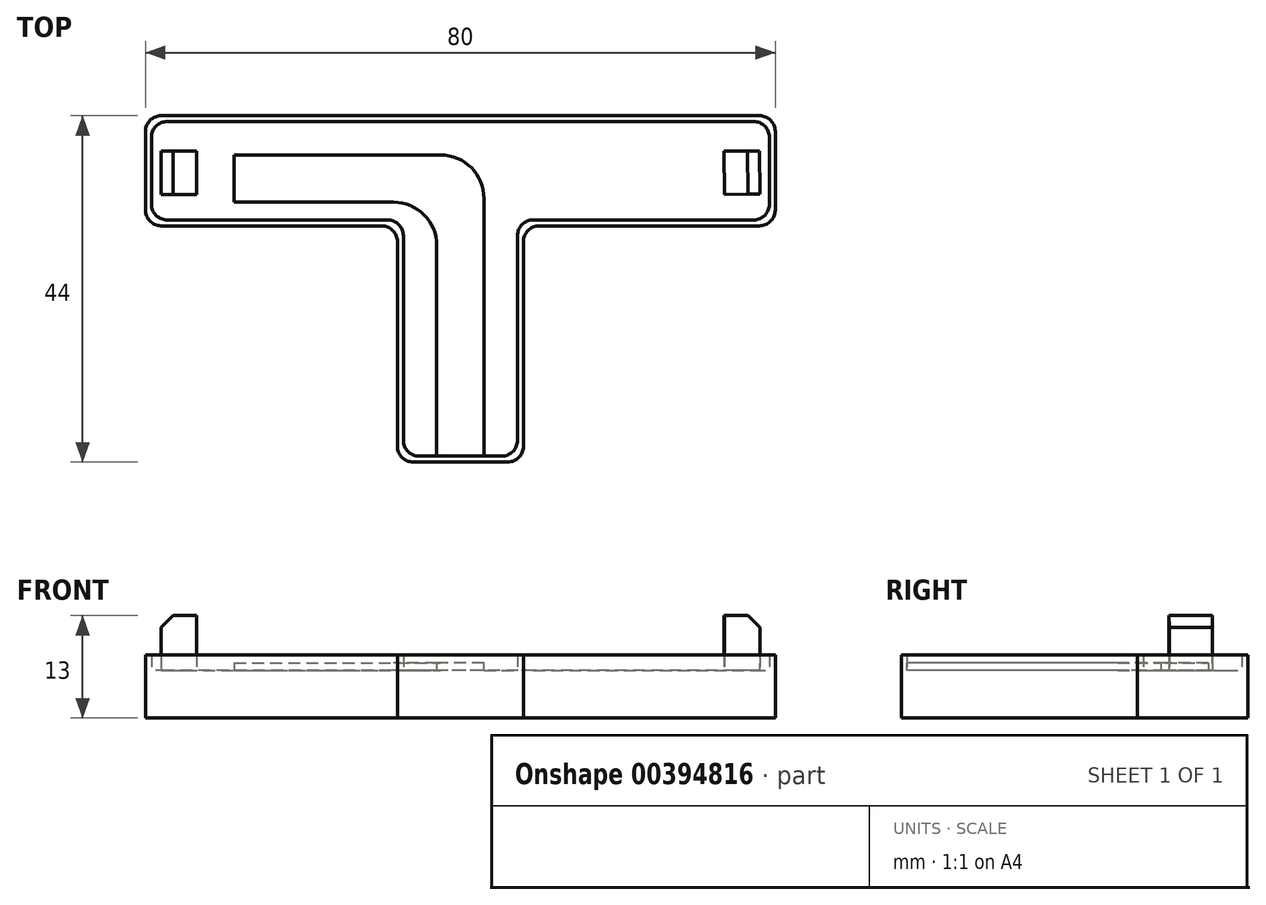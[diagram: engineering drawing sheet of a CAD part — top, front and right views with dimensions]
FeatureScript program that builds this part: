
annotation { "Feature Type Name" : "Feature", "Feature Type Description" : "" }
export const myFeature = defineFeature(function(context is Context, id is Id, definition is map)
    precondition{}
    {
        {
            var Q0;
            Q0=qCreatedBy(makeId("Top.planeOp"),FACE);
            var sketch = newSketch(context, id + "F0", { "sketchPlane" : qUnion([Q0])});
            skLineSegment(sketch, "E0", {"start": v(-12, 0) * mm, "end": v(-35, 0) * mm});
            skLineSegment(sketch, "E1", {"start": v(-37, 2) * mm, "end": v(-37, 12) * mm});
            skLineSegment(sketch, "E2", {"start": v(-35, 14) * mm, "end": v(35, 14) * mm});
            skLineSegment(sketch, "E3", {"start": v(37, 12) * mm, "end": v(37, 2) * mm});
            skLineSegment(sketch, "E4", {"start": v(6, -30) * mm, "end": v(-6, -30) * mm});
            skPoint(sketch, "E5.visualSharp", {"position": v(-37, 0) * mm});
            skArc(sketch, "E5.filletArc", {"start": v(-37, 2) * mm, "mid": v(-36.41, 0.59) * mm, "end": v(-35, 0) * mm});
            skPoint(sketch, "E6.visualSharp", {"position": v(-37, 14) * mm});
            skArc(sketch, "E6.filletArc", {"start": v(-35, 14) * mm, "mid": v(-36.41, 13.41) * mm, "end": v(-37, 12) * mm});
            skPoint(sketch, "E7.visualSharp", {"position": v(37, 14) * mm});
            skArc(sketch, "E7.filletArc", {"start": v(37, 12) * mm, "mid": v(36.41, 13.41) * mm, "end": v(35, 14) * mm});
            skPoint(sketch, "E8.visualSharp", {"position": v(37, 0) * mm});
            skArc(sketch, "E8.filletArc", {"start": v(35, 0) * mm, "mid": v(36.41, 0.59) * mm, "end": v(37, 2) * mm});
            skPoint(sketch, "E9.newPointA", {"position": v(0, 0) * mm});
            skPoint(sketch, "E10.newPointB", {"position": v(-10, 0) * mm});
            skLineSegment(sketch, "E11", {"start": v(-10, 0) * mm, "end": v(-38, 0) * mm});
            skLineSegment(sketch, "E12", {"start": v(-40, 2) * mm, "end": v(-40, 12) * mm});
            skLineSegment(sketch, "E13", {"start": v(-38, 14) * mm, "end": v(38, 14) * mm});
            skPoint(sketch, "E13.endSnap0", {"position": v(0, 14) * mm});
            skLineSegment(sketch, "E14", {"start": v(40, 12) * mm, "end": v(40, 2) * mm});
            skPoint(sketch, "E15.visualSharp", {"position": v(40, 14) * mm});
            skArc(sketch, "E15.filletArc", {"start": v(40, 12) * mm, "mid": v(39.41, 13.41) * mm, "end": v(38, 14) * mm});
            skPoint(sketch, "E16.visualSharp", {"position": v(40, 0) * mm});
            skArc(sketch, "E16.filletArc", {"start": v(38, 0) * mm, "mid": v(39.41, 0.59) * mm, "end": v(40, 2) * mm});
            skPoint(sketch, "E17.visualSharp", {"position": v(-40, 0) * mm});
            skArc(sketch, "E17.filletArc", {"start": v(-40, 2) * mm, "mid": v(-39.41, 0.59) * mm, "end": v(-38, 0) * mm});
            skPoint(sketch, "E18.visualSharp", {"position": v(-40, 14) * mm});
            skArc(sketch, "E18.filletArc", {"start": v(-38, 14) * mm, "mid": v(-39.41, 13.41) * mm, "end": v(-40, 12) * mm});
            skLineSegment(sketch, "E19", {"start": v(-10, 0) * mm, "end": v(-10, 0) * mm});
            skLineSegment(sketch, "E20", {"start": v(40, 0) * mm, "end": v(37, 0) * mm});
            skLineSegment(sketch, "E21", {"start": v(0, -30) * mm, "end": v(8, -30) * mm});
            skLineSegment(sketch, "E22", {"start": v(8, -28) * mm, "end": v(8, -2) * mm});
            skLineSegment(sketch, "E23.trimOffspring", {"start": v(35, 0) * mm, "end": v(38, 0) * mm});
            skLineSegment(sketch, "E24", {"start": v(10, 0) * mm, "end": v(38, 0) * mm});
            skArc(sketch, "E25.filletArc", {"start": v(10, 0) * mm, "mid": v(8.59, -0.59) * mm, "end": v(8, -2) * mm});
            skLineSegment(sketch, "E26", {"start": v(-8, -2) * mm, "end": v(-8, -28) * mm});
            skPoint(sketch, "E27.visualSharp", {"position": v(-8, -30) * mm});
            skArc(sketch, "E27.filletArc", {"start": v(-8, -28) * mm, "mid": v(-7.41, -29.41) * mm, "end": v(-6, -30) * mm});
            skPoint(sketch, "E28.visualSharp", {"position": v(8, -30) * mm});
            skArc(sketch, "E28.filletArc", {"start": v(6, -30) * mm, "mid": v(7.41, -29.41) * mm, "end": v(8, -28) * mm});
            skPoint(sketch, "E29.visualSharp", {"position": v(-8, 0) * mm});
            skArc(sketch, "E29.filletArc", {"start": v(-8, -2) * mm, "mid": v(-8.59, -0.59) * mm, "end": v(-10, 0) * mm});
            skSolve(sketch);
        }
        {
            var Q0;
            Q0 = qSketchRegion(id + "F0", true);
            extrude(context, id + "F1", {"entities" : qUnion([Q0]), "depth" : 6 * mm});
        }
        {
            var Q0;
            Q0=makeQuery(id+"F1.opExtrude","CAP_FACE",FACE,{"disambiguationData":[OSD([sQuery(id+"F0.wireOp",EDGE,"KrgK9lRR-1sEZ-YcQp-O3oG-SHxgb29owZ0h"),sQuery(id+"F0.wireOp",EDGE,"E0"),sQuery(id+"F0.wireOp",EDGE,"E1"),sQuery(id+"F0.wireOp",EDGE,"E2"),sQuery(id+"F0.wireOp",EDGE,"E3"),sQuery(id+"F0.wireOp",EDGE,"eoUHOFyy-lQIt-8kjD-7oxf-nCLPdvyQU6Ic"),sQuery(id+"F0.wireOp",EDGE,"2H0jnYMO-rJTe-XpiU-m9ek-4oq2zpUAxpcV"),sQuery(id+"F0.wireOp",EDGE,"E4"),sQuery(id+"F0.wireOp",EDGE,"E5.filletArc"),sQuery(id+"F0.wireOp",EDGE,"E6.filletArc"),sQuery(id+"F0.wireOp",EDGE,"E7.filletArc"),sQuery(id+"F0.wireOp",EDGE,"E8.filletArc"),sQuery(id+"F0.wireOp",EDGE,"E9.filletArc"),sQuery(id+"F0.wireOp",EDGE,"E10.filletArc"),sQuery(id+"F0.wireOp",EDGE,"4ed553e5-42bd-4c59-8323-b41fe6fd0794.filletArc"),sQuery(id+"F0.wireOp",EDGE,"28c6359a-0f53-4484-972b-61d877849d50.filletArc")])],"isStart":false});
            var sketch = newSketch(context, id + "F2", { "sketchPlane" : qUnion([Q0])});
            skPoint(sketch, "E30.visualSharp", {"position": v(-3, 9) * mm});
            skLineSegment(sketch, "E31", {"start": v(-3, -30) * mm, "end": v(3, -30) * mm});
            skLineSegment(sketch, "E32", {"start": v(-28.75, 9) * mm, "end": v(-2.5, 9) * mm});
            skLineSegment(sketch, "E33", {"start": v(-28.75, 3) * mm, "end": v(-8.5, 3) * mm});
            skLineSegment(sketch, "E34", {"start": v(3, 3.5) * mm, "end": v(3, -30) * mm});
            skLineSegment(sketch, "E35", {"start": v(-3, -2.5) * mm, "end": v(-3, -30) * mm});
            skLineSegment(sketch, "E36", {"start": v(3, -30) * mm, "end": v(-3, -30) * mm});
            skPoint(sketch, "E37.visualSharp", {"position": v(3, 9) * mm});
            skPoint(sketch, "E38.visualSharp", {"position": v(-3, 3) * mm});
            skLineSegment(sketch, "E39", {"start": v(-28.75, 9) * mm, "end": v(-28.75, 3) * mm});
            skPoint(sketch, "E40.orphan", {"position": v(-33, 3) * mm});
            skPoint(sketch, "E41.end.orphan", {"position": v(-33, 9) * mm});
            skArc(sketch, "E42", {"start": v(-7.98, 3) * mm, "mid": v(-7.98, 2.99) * mm, "end": v(-7.97, 2.97) * mm});
            skArc(sketch, "E43.trimOffspring", {"start": v(3, 3.5) * mm, "mid": v(1.39, 7.39) * mm, "end": v(-2.5, 9) * mm});
            skArc(sketch, "E44", {"start": v(-3, -2.5) * mm, "mid": v(-4.61, 1.39) * mm, "end": v(-8.5, 3) * mm});
            skSolve(sketch);
        }
        {
            var Q0;
            Q0=makeQuery(id+"F2.imprint","IMPRINT",FACE,{"disambiguationData":[TD([[makeQuery(id+"F2.imprint","IMPRINT",EDGE,{"derivedFrom":sQuery(id+"F2.wireOp",EDGE,"E32")}),-1.0]])]});
            extrude(context, id + "F3", {"entities" : qUnion([Q0]), "operationType" : NewBodyOperationType.ADD, "depth" : 1 * mm});
        }
        {
            var Q0;
            Q0=makeQuery(id+"F1.opExtrude","CAP_FACE",FACE,{"disambiguationData":[OSD([sQuery(id+"F0.wireOp",EDGE,"eoUHOFyy-lQIt-8kjD-7oxf-nCLPdvyQU6Ic"),sQuery(id+"F0.wireOp",EDGE,"2H0jnYMO-rJTe-XpiU-m9ek-4oq2zpUAxpcV"),sQuery(id+"F0.wireOp",EDGE,"E4"),sQuery(id+"F0.wireOp",EDGE,"E9.filletArc"),sQuery(id+"F0.wireOp",EDGE,"E10.filletArc"),sQuery(id+"F0.wireOp",EDGE,"4ed553e5-42bd-4c59-8323-b41fe6fd0794.filletArc"),sQuery(id+"F0.wireOp",EDGE,"28c6359a-0f53-4484-972b-61d877849d50.filletArc"),sQuery(id+"F0.wireOp",EDGE,"ouvHfpLu-oJne-QARU-IrEs-jNbR7pRuR2ui"),sQuery(id+"F0.wireOp",EDGE,"E11"),sQuery(id+"F0.wireOp",EDGE,"E12"),sQuery(id+"F0.wireOp",EDGE,"E13"),sQuery(id+"F0.wireOp",EDGE,"E14"),sQuery(id+"F0.wireOp",EDGE,"E15.filletArc"),sQuery(id+"F0.wireOp",EDGE,"E16.filletArc"),sQuery(id+"F0.wireOp",EDGE,"E17.filletArc"),sQuery(id+"F0.wireOp",EDGE,"E18.filletArc")])],"isStart":false});
            var sketch = newSketch(context, id + "F4", { "sketchPlane" : qUnion([Q0])});
            skLineSegment(sketch, "E45", {"start": v(0, 0) * mm, "end": v(35, 0) * mm});
            skLineSegment(sketch, "E46", {"start": v(35, 0) * mm, "end": v(40, 0) * mm});
            skLineSegment(sketch, "E47", {"start": v(40, 0) * mm, "end": v(38, 0) * mm});
            skPoint(sketch, "E48.endSnap0", {"position": v(38.04, 5.65) * mm});
            skLineSegment(sketch, "E49", {"start": v(38.04, 4.03) * mm, "end": v(35.24, 4) * mm});
            skPoint(sketch, "E50.orphan", {"position": v(37.9, 11.5) * mm});
            skLineSegment(sketch, "E51", {"start": v(38.04, 4.03) * mm, "end": v(37.97, 9.53) * mm});
            skLineSegment(sketch, "E52", {"start": v(37.97, 9.53) * mm, "end": v(35.17, 9.5) * mm});
            skLineSegment(sketch, "E53", {"start": v(0, 0) * mm, "end": v(-35, 0) * mm});
            skLineSegment(sketch, "E54", {"start": v(-35, 0) * mm, "end": v(-40.02, 0) * mm});
            skLineSegment(sketch, "E55", {"start": v(-40.02, 0) * mm, "end": v(-38.02, 0) * mm});
            skLineSegment(sketch, "E56", {"start": v(-38, 4) * mm, "end": v(-35.2, 4) * mm});
            skLineSegment(sketch, "E57", {"start": v(-38, 9.5) * mm, "end": v(-38, 4) * mm});
            skLineSegment(sketch, "E58", {"start": v(38.04, 4.03) * mm, "end": v(33.54, 3.98) * mm});
            skLineSegment(sketch, "E59", {"start": v(33.54, 3.98) * mm, "end": v(33.47, 9.48) * mm});
            skLineSegment(sketch, "E60", {"start": v(33.47, 9.48) * mm, "end": v(35.17, 9.5) * mm});
            skLineSegment(sketch, "E61", {"start": v(-38, 4) * mm, "end": v(-33.5, 4) * mm});
            skLineSegment(sketch, "E62", {"start": v(-33.5, 4) * mm, "end": v(-33.5, 9.5) * mm});
            skLineSegment(sketch, "E63", {"start": v(-33.5, 9.5) * mm, "end": v(-38, 9.5) * mm});
            skSolve(sketch);
        }
        {
            var Q0;
            Q0 = qSketchRegion(id + "F4", true);
            extrude(context, id + "F5", {"entities" : qUnion([Q0]), "operationType" : NewBodyOperationType.ADD, "depth" : 7 * mm});
        }
        {
            var Q0;
            Q0=makeQuery(id+"F2.imprint","IMPRINT",FACE,{"disambiguationData":[TD([[makeQuery(id+"F2.imprint","IMPRINT",EDGE,{"derivedFrom":sQuery(id+"F2.wireOp",EDGE,"E32")}),1.0]])]});
            var sketch = newSketch(context, id + "F6", { "sketchPlane" : qUnion([Q0])});
            skLineSegment(sketch, "E64", {"start": v(0, 0) * mm, "end": v(0, -30) * mm});
            skLineSegment(sketch, "E65", {"start": v(0, -30) * mm, "end": v(6, -30) * mm});
            skLineSegment(sketch, "E66", {"start": v(8, -28) * mm, "end": v(8, -2) * mm});
            skLineSegment(sketch, "E67", {"start": v(10, 0) * mm, "end": v(38, 0) * mm});
            skLineSegment(sketch, "E68", {"start": v(40, 2) * mm, "end": v(40, 12) * mm});
            skLineSegment(sketch, "E69", {"start": v(38, 14) * mm, "end": v(-38, 14) * mm});
            skLineSegment(sketch, "E70", {"start": v(-40, 12) * mm, "end": v(-40, 2) * mm});
            skLineSegment(sketch, "E71", {"start": v(-38, 0) * mm, "end": v(-10, 0) * mm});
            skLineSegment(sketch, "E72", {"start": v(-8, -2) * mm, "end": v(-8, -28) * mm});
            skLineSegment(sketch, "E73", {"start": v(-6, -30) * mm, "end": v(0, -30) * mm});
            skLineSegment(sketch, "E74", {"start": v(8, 0) * mm, "end": v(7.25, 0) * mm});
            skLineSegment(sketch, "E75", {"start": v(7.25, -1.25) * mm, "end": v(7.25, -27.25) * mm});
            skLineSegment(sketch, "E76", {"start": v(0, -30) * mm, "end": v(0, -29.25) * mm});
            skLineSegment(sketch, "E77", {"start": v(0, -29.25) * mm, "end": v(5.25, -29.25) * mm});
            skLineSegment(sketch, "E78", {"start": v(9.25, 0.75) * mm, "end": v(37.25, 0.75) * mm});
            skLineSegment(sketch, "E79", {"start": v(40, 0) * mm, "end": v(39.25, 0) * mm});
            skLineSegment(sketch, "E80", {"start": v(39.25, 2.75) * mm, "end": v(39.25, 11.25) * mm});
            skLineSegment(sketch, "E81", {"start": v(23.7, 13.25) * mm, "end": v(37.25, 13.25) * mm});
            skLineSegment(sketch, "E82", {"start": v(23.7, 13.25) * mm, "end": v(-37.25, 13.25) * mm});
            skLineSegment(sketch, "E83", {"start": v(-39.25, 11.25) * mm, "end": v(-39.25, 2.75) * mm});
            skLineSegment(sketch, "E84", {"start": v(-28.47, 0.75) * mm, "end": v(-37.25, 0.75) * mm});
            skLineSegment(sketch, "E85", {"start": v(-28.47, 0.75) * mm, "end": v(-9.25, 0.75) * mm});
            skLineSegment(sketch, "E86", {"start": v(0, -29.25) * mm, "end": v(-5.25, -29.25) * mm});
            skLineSegment(sketch, "E87", {"start": v(-7.25, -16.29) * mm, "end": v(-7.25, -1.25) * mm});
            skLineSegment(sketch, "E88", {"start": v(-7.25, -16.29) * mm, "end": v(-7.25, -27.25) * mm});
            skArc(sketch, "E89.filletArc", {"start": v(5.25, -29.25) * mm, "mid": v(6.66, -28.66) * mm, "end": v(7.25, -27.25) * mm});
            skPoint(sketch, "E90.visualSharp", {"position": v(8, -30) * mm});
            skArc(sketch, "E90.filletArc", {"start": v(6, -30) * mm, "mid": v(7.41, -29.41) * mm, "end": v(8, -28) * mm});
            skPoint(sketch, "E91.visualSharp", {"position": v(8, 0) * mm});
            skArc(sketch, "E91.filletArc", {"start": v(10, 0) * mm, "mid": v(8.59, -0.59) * mm, "end": v(8, -2) * mm});
            skArc(sketch, "E92.filletArc", {"start": v(9.25, 0.75) * mm, "mid": v(7.84, 0.16) * mm, "end": v(7.25, -1.25) * mm});
            skArc(sketch, "E93.filletArc", {"start": v(37.25, 0.75) * mm, "mid": v(38.66, 1.34) * mm, "end": v(39.25, 2.75) * mm});
            skPoint(sketch, "E94.visualSharp", {"position": v(40, 0) * mm});
            skArc(sketch, "E94.filletArc", {"start": v(38, 0) * mm, "mid": v(39.41, 0.59) * mm, "end": v(40, 2) * mm});
            skArc(sketch, "E95.filletArc", {"start": v(39.25, 11.25) * mm, "mid": v(38.66, 12.66) * mm, "end": v(37.25, 13.25) * mm});
            skPoint(sketch, "E96.visualSharp", {"position": v(40, 14) * mm});
            skArc(sketch, "E96.filletArc", {"start": v(40, 12) * mm, "mid": v(39.41, 13.41) * mm, "end": v(38, 14) * mm});
            skArc(sketch, "E97.filletArc", {"start": v(-37.25, 13.25) * mm, "mid": v(-38.66, 12.66) * mm, "end": v(-39.25, 11.25) * mm});
            skPoint(sketch, "E98.visualSharp", {"position": v(-40, 14) * mm});
            skArc(sketch, "E98.filletArc", {"start": v(-38, 14) * mm, "mid": v(-39.41, 13.41) * mm, "end": v(-40, 12) * mm});
            skArc(sketch, "E99.filletArc", {"start": v(-39.25, 2.75) * mm, "mid": v(-38.66, 1.34) * mm, "end": v(-37.25, 0.75) * mm});
            skPoint(sketch, "E100.visualSharp", {"position": v(-40, 0) * mm});
            skArc(sketch, "E100.filletArc", {"start": v(-40, 2) * mm, "mid": v(-39.41, 0.59) * mm, "end": v(-38, 0) * mm});
            skPoint(sketch, "E101.visualSharp", {"position": v(-8, 0) * mm});
            skArc(sketch, "E101.filletArc", {"start": v(-8, -2) * mm, "mid": v(-8.59, -0.59) * mm, "end": v(-10, 0) * mm});
            skArc(sketch, "E102.filletArc", {"start": v(-7.25, -1.25) * mm, "mid": v(-7.84, 0.16) * mm, "end": v(-9.25, 0.75) * mm});
            skArc(sketch, "E103.filletArc", {"start": v(-7.25, -27.25) * mm, "mid": v(-6.66, -28.66) * mm, "end": v(-5.25, -29.25) * mm});
            skPoint(sketch, "E104.visualSharp", {"position": v(-8, -30) * mm});
            skArc(sketch, "E104.filletArc", {"start": v(-8, -28) * mm, "mid": v(-7.41, -29.41) * mm, "end": v(-6, -30) * mm});
            skLineSegment(sketch, "E105", {"start": v(-5.25, -29.25) * mm, "end": v(5.25, -29.25) * mm});
            skSolve(sketch);
        }
        {
            var Q0;
            Q0 = qSketchRegion(id + "F6", true);
            extrude(context, id + "F7", {"entities" : qUnion([Q0]), "operationType" : NewBodyOperationType.ADD, "depth" : 2 * mm});
        }
        {
            var Q0;
            Q0=makeQuery(id+"F5.opExtrude","SWEPT_FACE",FACE,{"disambiguationData":[OSD([sQuery(id+"F4.wireOp",EDGE,"E58")])]});
            var sketch = newSketch(context, id + "F8", { "sketchPlane" : qUnion([Q0])});
            skLineSegment(sketch, "E106", {"start": v(33.58, 6) * mm, "end": v(33.58, 13) * mm});
            skLineSegment(sketch, "E107", {"start": v(33.58, 13) * mm, "end": v(38.08, 13) * mm});
            skLineSegment(sketch, "E108", {"start": v(33.58, 6) * mm, "end": v(38.08, 6) * mm});
            skLineSegment(sketch, "E109", {"start": v(38.08, 6) * mm, "end": v(38.08, 13) * mm});
            skLineSegment(sketch, "E110", {"start": v(38.08, 6) * mm, "end": v(36.08, 6) * mm});
            skLineSegment(sketch, "E111", {"start": v(36.08, 6) * mm, "end": v(36.08, 10) * mm});
            skLineSegment(sketch, "E112", {"start": v(36.08, 10) * mm, "end": v(38.08, 10) * mm});
            skLineSegment(sketch, "E113", {"start": v(38.08, 10) * mm, "end": v(38.08, 11.5) * mm});
            skLineSegment(sketch, "E114", {"start": v(38.08, 11.5) * mm, "end": v(36.58, 13) * mm});
            skLineSegment(sketch, "E115", {"start": v(38.08, 6) * mm, "end": v(38.08, 10) * mm});
            skSolve(sketch);
        }
        {
            var Q0;
            {var subQ0=sQuery(id+"F8.wireOp",EDGE,"E109");Q0=makeQuery(id+"F8.imprint","IMPRINT",FACE,{"disambiguationData":[TD([[makeQuery(id+"F8.imprint","IMPRINT",EDGE,{"derivedFrom":subQ0}),-1.0]])]});}
            var Q1;
            Q1=makeQuery(id+"F8.imprint","IMPRINT",FACE,{"disambiguationData":[TD([[makeQuery(id+"F8.imprint","IMPRINT",EDGE,{"derivedFrom":sQuery(id+"F8.wireOp",EDGE,"E110")}),-1.0]])]});
            extrude(context, id + "F9", {"entities" : qUnion([Q0, Q1]), "operationType" : NewBodyOperationType.REMOVE, "oppositeDirection" : true, "depth" : 6 * mm});
        }
        {
            var Q0;
            Q0=makeQuery(id+"F5.opExtrude","SWEPT_FACE",FACE,{"disambiguationData":[OSD([sQuery(id+"F4.wireOp",EDGE,"E61")])]});
            var sketch = newSketch(context, id + "F10", { "sketchPlane" : qUnion([Q0])});
            skLineSegment(sketch, "E116", {"start": v(-33.5, 6) * mm, "end": v(-33.5, 13) * mm});
            skLineSegment(sketch, "E117", {"start": v(-33.5, 13) * mm, "end": v(-38, 13) * mm});
            skLineSegment(sketch, "E118", {"start": v(-38, 13) * mm, "end": v(-38, 6) * mm});
            skLineSegment(sketch, "E119", {"start": v(-38, 6) * mm, "end": v(-33.5, 6) * mm});
            skLineSegment(sketch, "E120", {"start": v(-38, 6) * mm, "end": v(-36, 6) * mm});
            skLineSegment(sketch, "E121", {"start": v(-36, 6) * mm, "end": v(-36, 10) * mm});
            skLineSegment(sketch, "E122", {"start": v(-36, 10) * mm, "end": v(-38, 10) * mm});
            skLineSegment(sketch, "E123", {"start": v(-38, 10) * mm, "end": v(-38, 11.5) * mm});
            skLineSegment(sketch, "E124", {"start": v(-38, 11.5) * mm, "end": v(-36.5, 13) * mm});
            skLineSegment(sketch, "E125", {"start": v(-36.5, 13) * mm, "end": v(-38, 13) * mm});
            skLineSegment(sketch, "E126", {"start": v(-38, 11.5) * mm, "end": v(-38, 13) * mm});
            skLineSegment(sketch, "E127", {"start": v(-36.5, 13) * mm, "end": v(-33.5, 13) * mm});
            skLineSegment(sketch, "E128", {"start": v(-38, 10) * mm, "end": v(-38, 6) * mm});
            skSolve(sketch);
        }
        {
            var Q0;
            Q0=makeQuery(id+"F10.imprint","IMPRINT",FACE,{"disambiguationData":[TD([[makeQuery(id+"F10.imprint","IMPRINT",EDGE,{"derivedFrom":sQuery(id+"F10.wireOp",EDGE,"E120")}),1.0]])]});
            var Q1;
            Q1=makeQuery(id+"F10.imprint","IMPRINT",FACE,{"disambiguationData":[TD([[makeQuery(id+"F10.imprint","IMPRINT",EDGE,{"derivedFrom":sQuery(id+"F10.wireOp",EDGE,"E124")}),1.0]])]});
            extrude(context, id + "F11", {"entities" : qUnion([Q0, Q1]), "operationType" : NewBodyOperationType.REMOVE, "oppositeDirection" : true, "depth" : 6 * mm});
        }
    });
